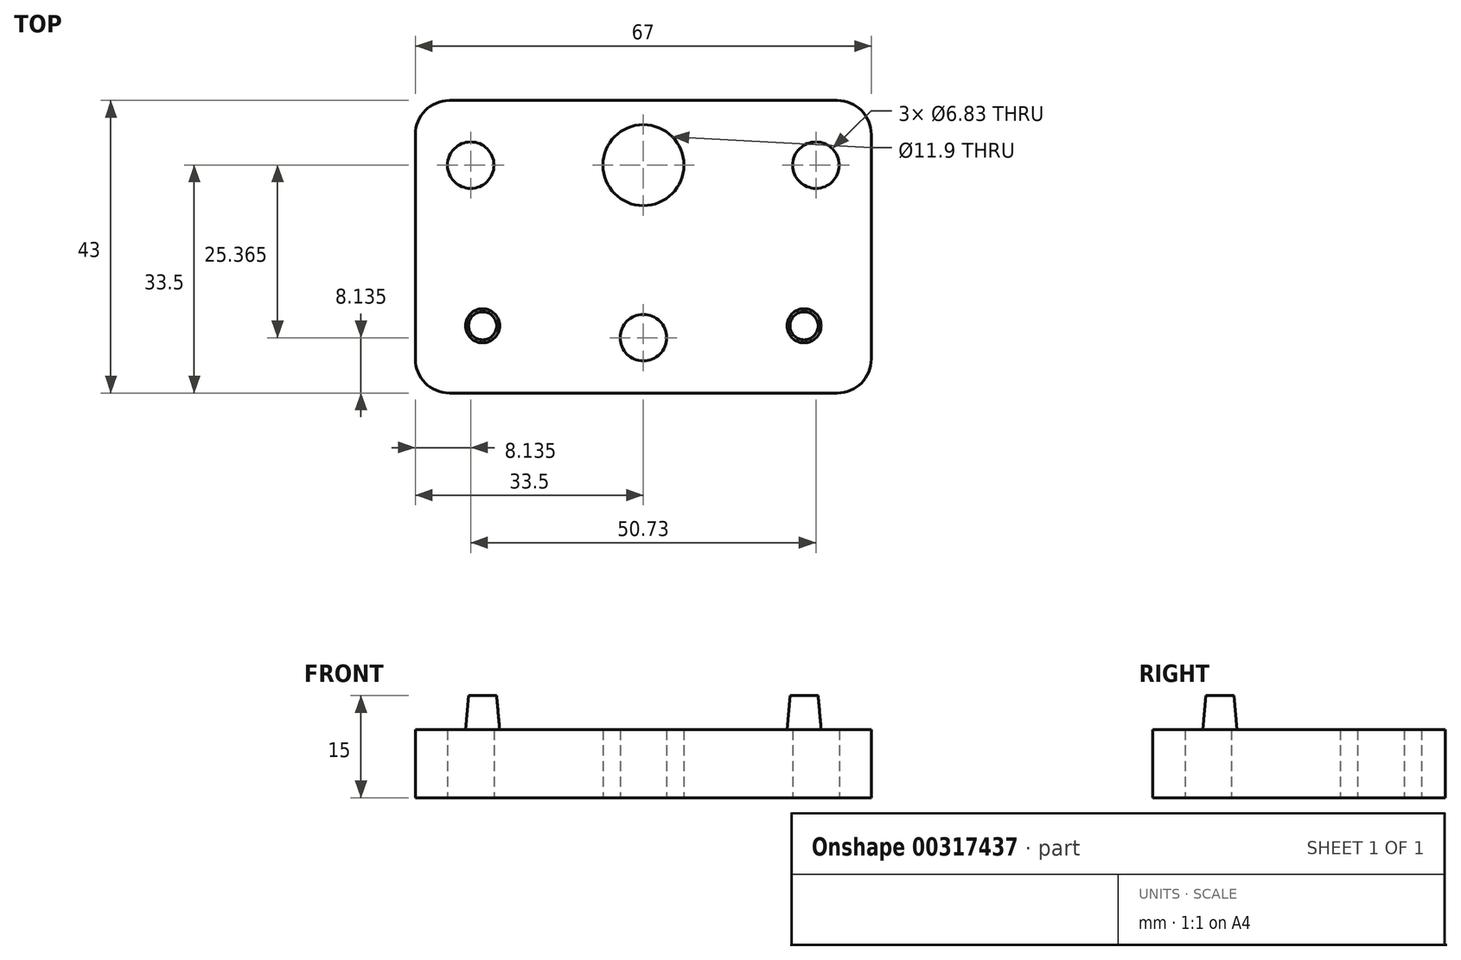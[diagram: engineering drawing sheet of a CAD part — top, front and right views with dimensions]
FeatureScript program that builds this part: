
annotation { "Feature Type Name" : "Feature", "Feature Type Description" : "" }
export const myFeature = defineFeature(function(context is Context, id is Id, definition is map)
    precondition{}
    {
        {
            var Q0;
            Q0=qCreatedBy(makeId("Top.planeOp"),FACE);
            var sketch = newSketch(context, id + "F0", { "sketchPlane" : qUnion([Q0])});
            skLineSegment(sketch, "E0.bottom", {"start": v(-33.5, 9.5) * mm, "end": v(33.5, 9.5) * mm});
            skLineSegment(sketch, "E0.top", {"start": v(-33.5, -33.5) * mm, "end": v(33.5, -33.5) * mm});
            skLineSegment(sketch, "E0.left", {"start": v(-33.5, 9.5) * mm, "end": v(-33.5, -33.5) * mm});
            skLineSegment(sketch, "E0.right", {"start": v(33.5, 9.5) * mm, "end": v(33.5, -33.5) * mm});
            skCircle(sketch, "E1", {"center": v(0, 0) * mm, "radius": 5.95 * mm});
            skCircle(sketch, "E2", {"center": v(25.37, 0) * mm, "radius": 3.42 * mm});
            skCircle(sketch, "E3", {"center": v(-25.37, 0) * mm, "radius": 3.42 * mm});
            skLineSegment(sketch, "E4.bottom", {"start": v(-14.98, 9.5) * mm, "end": v(14.98, 9.5) * mm});
            skLineSegment(sketch, "E4.top", {"start": v(-14.98, -33.5) * mm, "end": v(14.98, -33.5) * mm});
            skLineSegment(sketch, "E4.left", {"start": v(-14.98, 9.5) * mm, "end": v(-14.98, -33.5) * mm});
            skLineSegment(sketch, "E4.right", {"start": v(14.98, 9.5) * mm, "end": v(14.98, -33.5) * mm});
            skCircle(sketch, "E5", {"center": v(-25.37, 0) * mm, "radius": 5.42 * mm});
            skCircle(sketch, "E6", {"center": v(25.37, 0) * mm, "radius": 5.42 * mm});
            skCircle(sketch, "E7", {"center": v(0, -25.37) * mm, "radius": 3.42 * mm});
            skCircle(sketch, "E8", {"center": v(0, -25.37) * mm, "radius": 5.42 * mm});
            skSolve(sketch);
        }
        {
            var Q0;
            Q0=makeQuery(id+"F0.imprint","IMPRINT",FACE,{"disambiguationData":[TD([[makeQuery(id+"F0.imprint","IMPRINT",EDGE,{"derivedFrom":sQuery(id+"F0.wireOp",EDGE,"E1")}),-1.0]])]});
            extrude(context, id + "F1", {"entities" : qUnion([Q0]), "offsetDistance" : 25 * mm, "depth" : 10 * mm});
        }
        {
            var Q0;
            {var subQ1=sQuery(id+"F0.wireOp",EDGE,"E0.left");Q0=makeQuery(id+"F0.imprint","IMPRINT",FACE,{"disambiguationData":[TD([[makeQuery(id+"F0.imprint","IMPRINT",EDGE,{"derivedFrom":subQ1}),1.0]])]});}
            var Q1;
            {var subQ1=sQuery(id+"F0.wireOp",EDGE,"E0.right");Q1=makeQuery(id+"F0.imprint","IMPRINT",FACE,{"disambiguationData":[TD([[makeQuery(id+"F0.imprint","IMPRINT",EDGE,{"derivedFrom":subQ1}),-1.0]])]});}
            extrude(context, id + "F2", {"entities" : qUnion([Q0, Q1]), "operationType" : NewBodyOperationType.ADD, "depth" : 10 * mm});
        }
        {
            var Q0;
            Q0=makeQuery(id+"F0.imprint","IMPRINT",FACE,{"disambiguationData":[TD([[makeQuery(id+"F0.imprint","IMPRINT",EDGE,{"derivedFrom":sQuery(id+"F0.wireOp",EDGE,"E3")}),-1.0]])]});
            var Q1;
            Q1=makeQuery(id+"F0.imprint","IMPRINT",FACE,{"disambiguationData":[TD([[makeQuery(id+"F0.imprint","IMPRINT",EDGE,{"derivedFrom":sQuery(id+"F0.wireOp",EDGE,"E2")}),-1.0]])]});
            var Q2;
            Q2=makeQuery(id+"F0.imprint","IMPRINT",FACE,{"disambiguationData":[TD([[makeQuery(id+"F0.imprint","IMPRINT",EDGE,{"derivedFrom":sQuery(id+"F0.wireOp",EDGE,"E7")}),-1.0]])]});
            extrude(context, id + "F3", {"entities" : qUnion([Q0, Q1, Q2]), "operationType" : NewBodyOperationType.ADD, "depth" : 10 * mm});
        }
        {
            var Q0;
            {var subQ0=sQuery(id+"F0.wireOp",EDGE,"E4.right");Q0=makeQuery(id+"F0.imprint","IMPRINT",FACE,{"disambiguationData":[TD([[makeQuery(id+"F0.imprint","IMPRINT",EDGE,{"derivedFrom":subQ0}),1.0]])]});}
            var Q1;
            {var subQ0=sQuery(id+"F0.wireOp",EDGE,"E4.left");Q1=makeQuery(id+"F0.imprint","IMPRINT",FACE,{"disambiguationData":[TD([[makeQuery(id+"F0.imprint","IMPRINT",EDGE,{"derivedFrom":subQ0}),-1.0]])]});}
            extrude(context, id + "F4", {"entities" : qUnion([Q0, Q1]), "operationType" : NewBodyOperationType.ADD, "depth" : 10 * mm});
        }
        {
            var Q0;
            Q0=qCreatedBy(makeId("Top.planeOp"),FACE);
            var sketch = newSketch(context, id + "F5", { "sketchPlane" : qUnion([Q0])});
            skLineSegment(sketch, "E9.rect.bottom", {"start": v(-28.11, 28.11) * mm, "end": v(28.12, 28.11) * mm});
            skLineSegment(sketch, "E9.rect.top", {"start": v(-28.12, -28.11) * mm, "end": v(28.11, -28.11) * mm});
            skLineSegment(sketch, "E9.rect.left", {"start": v(-28.11, 28.12) * mm, "end": v(-28.12, -28.11) * mm});
            skLineSegment(sketch, "E9.rect.right", {"start": v(28.12, 28.12) * mm, "end": v(28.11, -28.11) * mm});
            skPoint(sketch, "E9.rect.middle", {"position": v(0, 0) * mm});
            skCircle(sketch, "E10", {"center": v(0, 0) * mm, "radius": 19.04 * mm});
            skCircle(sketch, "E11", {"center": v(0, 0) * mm, "radius": 3.98 * mm});
            skCircle(sketch, "E12", {"center": v(-23.62, 23.62) * mm, "radius": 2.5 * mm});
            skCircle(sketch, "E13", {"center": v(23.62, 23.62) * mm, "radius": 2.5 * mm});
            skCircle(sketch, "E14", {"center": v(23.62, -23.62) * mm, "radius": 2.5 * mm});
            skCircle(sketch, "E15", {"center": v(-23.62, -23.62) * mm, "radius": 2.5 * mm});
            skLineSegment(sketch, "E16.rect.bottom", {"start": v(-23.62, 23.62) * mm, "end": v(23.62, 23.62) * mm, "construction": true});
            skLineSegment(sketch, "E16.rect.top", {"start": v(-23.62, -23.62) * mm, "end": v(23.62, -23.62) * mm, "construction": true});
            skLineSegment(sketch, "E16.rect.left", {"start": v(-23.62, 23.62) * mm, "end": v(-23.62, -23.62) * mm, "construction": true});
            skLineSegment(sketch, "E16.rect.right", {"start": v(23.62, 23.62) * mm, "end": v(23.62, -23.62) * mm, "construction": true});
            skCircle(sketch, "E17", {"center": v(0, 0) * mm, "radius": 5.38 * mm});
            skSolve(sketch);
        }
        {
            var Q0;
            {var subQ0=sQuery(id+"F0.wireOp",EDGE,"E8");var subQ1=sQuery(id+"F0.wireOp",EDGE,"E5");var subQ2=sQuery(id+"F0.wireOp",EDGE,"E6");var subQ3=sQuery(id+"F0.wireOp",EDGE,"E4.right");var subQ4=sQuery(id+"F0.wireOp",EDGE,"E0.top");var subQ5=sQuery(id+"F0.wireOp",EDGE,"E0.bottom");var subQ6=sQuery(id+"F0.wireOp",EDGE,"E4.left");Q0=makeQuery(id+"F3.boolean.opBoolean","MERGE",FACE,{"derivedFrom":[makeQuery(id+"F2.boolean.opBoolean","MERGE",FACE,{"derivedFrom":[makeQuery(id+"F1.opExtrude","CAP_FACE",FACE,{"disambiguationData":[OSD([sQuery(id+"F0.wireOp",EDGE,"E1"),sQuery(id+"F0.wireOp",EDGE,"E4.bottom"),sQuery(id+"F0.wireOp",EDGE,"E4.top"),subQ6,subQ3,subQ0])],"isStart":false}),makeQuery(id+"F2.opExtrude","CAP_FACE",FACE,{"disambiguationData":[OSD([subQ5,subQ4,sQuery(id+"F0.wireOp",EDGE,"E0.left"),subQ6,subQ1])],"isStart":false}),makeQuery(id+"F2.opExtrude","CAP_FACE",FACE,{"disambiguationData":[OSD([subQ5,subQ4,sQuery(id+"F0.wireOp",EDGE,"E0.right"),subQ3,subQ2])],"isStart":false})]}),makeQuery(id+"F3.opExtrude","CAP_FACE",FACE,{"disambiguationData":[OSD([sQuery(id+"F0.wireOp",EDGE,"E2"),subQ2])],"isStart":false}),makeQuery(id+"F3.opExtrude","CAP_FACE",FACE,{"disambiguationData":[OSD([sQuery(id+"F0.wireOp",EDGE,"E3"),subQ1])],"isStart":false}),makeQuery(id+"F3.opExtrude","CAP_FACE",FACE,{"disambiguationData":[OSD([sQuery(id+"F0.wireOp",EDGE,"E7"),subQ0])],"isStart":false})]});}
            var sketch = newSketch(context, id + "F6", { "sketchPlane" : qUnion([Q0])});
            skCircle(sketch, "E18", {"center": v(-23.62, -23.62) * mm, "radius": 2.5 * mm});
            skCircle(sketch, "E19", {"center": v(23.62, -23.62) * mm, "radius": 2.5 * mm});
            skSolve(sketch);
        }
        {
            var Q0;
            Q0=qSketchRegion(id+"F6",true);
            extrude(context, id + "F7", {"entities" : qUnion([Q0]), "operationType" : NewBodyOperationType.ADD, "depth" : 5 * mm, "hasDraft" : true, "draftAngle" : 5 * degree, "draftPullDirection" : true});
        }
        {
            var Q0;
            Q0=makeQuery(id+"F2.opExtrude","SWEPT_EDGE",EDGE,{"disambiguationData":[OSD([sQuery(id+"F0.wireOp",EDGE,"E0.top"),sQuery(id+"F0.wireOp",EDGE,"E0.left")])]});
            var Q1;
            Q1=makeQuery(id+"F2.opExtrude","SWEPT_EDGE",EDGE,{"disambiguationData":[OSD([sQuery(id+"F0.wireOp",EDGE,"E0.top"),sQuery(id+"F0.wireOp",EDGE,"E0.right")])]});
            var Q2;
            Q2=makeQuery(id+"F2.opExtrude","SWEPT_EDGE",EDGE,{"disambiguationData":[OSD([sQuery(id+"F0.wireOp",EDGE,"E0.bottom"),sQuery(id+"F0.wireOp",EDGE,"E0.right")])]});
            var Q3;
            Q3=makeQuery(id+"F2.opExtrude","SWEPT_EDGE",EDGE,{"disambiguationData":[OSD([sQuery(id+"F0.wireOp",EDGE,"E0.bottom"),sQuery(id+"F0.wireOp",EDGE,"E0.left")])]});
            fillet(context, id + "F8", {"entities" : qUnion([Q0, Q1, Q2, Q3]), "radius" : 5 * mm, "tangentPropagation" : true, "allowEdgeOverflow" : false});
        }
    });
